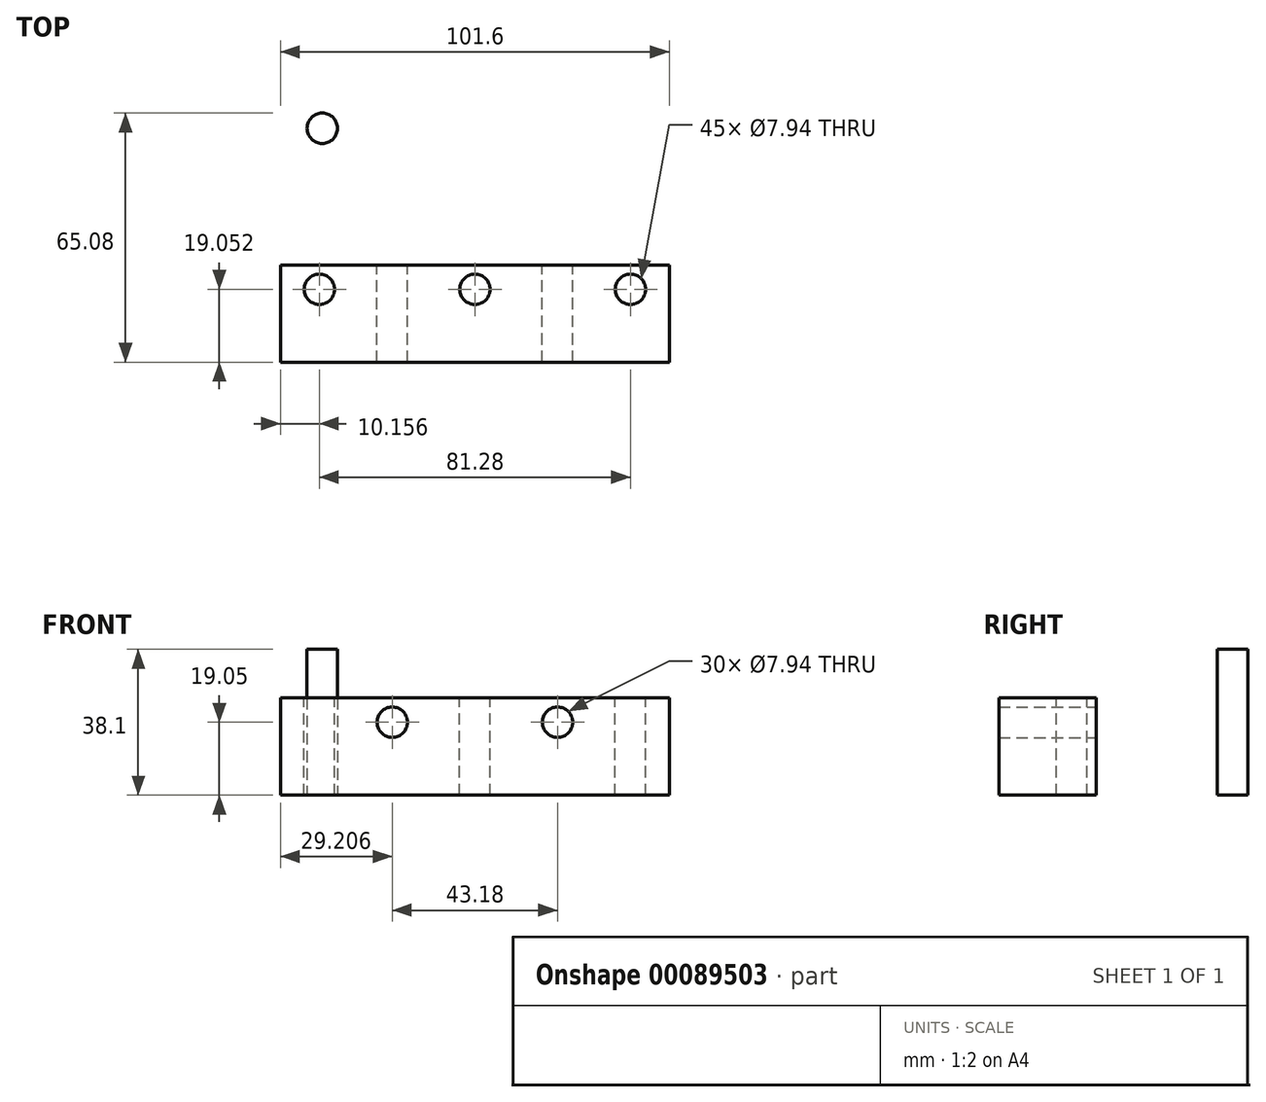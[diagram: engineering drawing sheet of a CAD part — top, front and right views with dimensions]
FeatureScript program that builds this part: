
annotation { "Feature Type Name" : "Feature", "Feature Type Description" : "" }
export const myFeature = defineFeature(function(context is Context, id is Id, definition is map)
    precondition{}
    {
        {
            var Q0;
            Q0=qCreatedBy(makeId("Top.planeOp"),FACE);
            var sketch = newSketch(context, id + "F0", { "sketchPlane" : qUnion([Q0])});
            skLineSegment(sketch, "E0.bottom", {"start": v(-45.27, 11.95) * mm, "end": v(56.33, 11.95) * mm});
            skLineSegment(sketch, "E0.top", {"start": v(-45.27, -13.45) * mm, "end": v(56.33, -13.45) * mm});
            skLineSegment(sketch, "E0.left", {"start": v(-45.27, 11.95) * mm, "end": v(-45.27, -13.45) * mm});
            skLineSegment(sketch, "E0.right", {"start": v(56.33, 11.95) * mm, "end": v(56.33, -13.45) * mm});
            skSolve(sketch);
        }
        {
            var Q0;
            Q0=makeQuery(id+"F0.imprint","IMPRINT",FACE,{"disambiguationData":[TD([[makeQuery(id+"F0.imprint","IMPRINT",EDGE,{"derivedFrom":sQuery(id+"F0.wireOp",EDGE,"E0.bottom")}),-1.0]])]});
            extrude(context, id + "F1", {"entities" : qUnion([Q0]), "depth" : 25.4 * mm});
        }
        {
            var Q0;
            Q0=makeQuery(id+"F1.opExtrude","CAP_FACE",FACE,{"disambiguationData":[OSD([sQuery(id+"F0.wireOp",EDGE,"E0.bottom"),sQuery(id+"F0.wireOp",EDGE,"E0.top"),sQuery(id+"F0.wireOp",EDGE,"E0.left"),sQuery(id+"F0.wireOp",EDGE,"E0.right")])],"isStart":false});
            var sketch = newSketch(context, id + "F2", { "sketchPlane" : qUnion([Q0])});
            skLineSegment(sketch, "E1", {"start": v(-45.27, -0.75) * mm, "end": v(56.33, -0.75) * mm, "construction": true});
            skPoint(sketch, "E2", {"position": v(-35.11, 5.6) * mm});
            skPoint(sketch, "E3", {"position": v(46.17, 5.6) * mm});
            skPoint(sketch, "E4", {"position": v(5.53, 5.6) * mm});
            skSolve(sketch);
        }
        {
            var Q0;
            Q0=sQuery(id+"F2.wireOp",VERTEX,"E2");
            var Q1;
            Q1=sQuery(id+"F2.wireOp",VERTEX,"E4");
            var Q2;
            Q2=sQuery(id+"F2.wireOp",VERTEX,"E3");
            var Q3;
            Q3=makeQuery(id+"F1.opExtrude","SWEPT_BODY",BODY,{"disambiguationData":[OSD([sQuery(id+"F0.wireOp",EDGE,"E0.bottom"),sQuery(id+"F0.wireOp",EDGE,"E0.top"),sQuery(id+"F0.wireOp",EDGE,"E0.left"),sQuery(id+"F0.wireOp",EDGE,"E0.right")])]});
            hole(context, id + "F3", {"style" : HoleStyle.SIMPLE, "endStyle" : HoleEndStyle.THROUGH, "holeDiameter" : 7.94 * mm, "locations" : qUnion([Q0, Q1, Q2]), "scope" : qUnion([Q3]), "isTappedThrough" : true});
        }
        {
            var Q0;
            Q0=qCreatedBy(makeId("Top.planeOp"),FACE);
            var sketch = newSketch(context, id + "F4", { "sketchPlane" : qUnion([Q0])});
            skCircle(sketch, "E5", {"center": v(-34.35, 47.66) * mm, "radius": 3.97 * mm});
            skSolve(sketch);
        }
        {
            var Q0;
            Q0=makeQuery(id+"F4.imprint","IMPRINT",FACE,{"disambiguationData":[TD([[makeQuery(id+"F4.imprint","IMPRINT",EDGE,{"derivedFrom":sQuery(id+"F4.wireOp",EDGE,"E5")}),1.0]])]});
            var Q1;
            Q1=sQuery(id+"F4.wireOp",EDGE,"E5");
            extrude(context, id + "F5", {"entities" : qUnion([Q0]), "surfaceEntities" : qUnion([Q1]), "depth" : 38.1 * mm});
        }
        {
            var Q0;
            Q0=makeQuery(id+"F1.opExtrude","SWEPT_FACE",FACE,{"disambiguationData":[OSD([sQuery(id+"F0.wireOp",EDGE,"E0.bottom")])]});
            var sketch = newSketch(context, id + "F6", { "sketchPlane" : qUnion([Q0])});
            skPoint(sketch, "E6", {"position": v(16.06, 19.05) * mm});
            skPoint(sketch, "E7", {"position": v(-27.12, 19.05) * mm});
            skSolve(sketch);
        }
        {
            var Q0;
            Q0=sQuery(id+"F6.wireOp",VERTEX,"E6");
            var Q1;
            Q1=sQuery(id+"F6.wireOp",VERTEX,"E7");
            var Q2;
            Q2=makeQuery(id+"F1.opExtrude","SWEPT_BODY",BODY,{"disambiguationData":[OSD([sQuery(id+"F0.wireOp",EDGE,"E0.bottom"),sQuery(id+"F0.wireOp",EDGE,"E0.top"),sQuery(id+"F0.wireOp",EDGE,"E0.left"),sQuery(id+"F0.wireOp",EDGE,"E0.right")])]});
            hole(context, id + "F7", {"style" : HoleStyle.SIMPLE, "endStyle" : HoleEndStyle.THROUGH, "holeDiameter" : 7.94 * mm, "locations" : qUnion([Q0, Q1]), "scope" : qUnion([Q2]), "isTappedThrough" : true});
        }
    });
